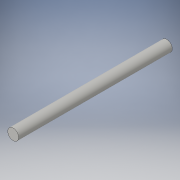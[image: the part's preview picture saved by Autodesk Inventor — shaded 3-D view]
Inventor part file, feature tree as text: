
AUTODESK INVENTOR PART (.ipt)
format: ipt  version: 2016 (Build 200138000, 138)  size: 86,528 bytes
history: native  units: in
note: dims shown in document units (in); Inventor stores cm internally (conversion verified against a paired STEP export)
features: extrude x1, sketch x1
ambient origin geometry x8: Origin, YZ Plane, XZ Plane, XY Plane, X Axis, Y Axis, Z Axis, Center Point
bodies: Solid1 (feature_tree)
feature tree (2):
  extrude  "Extrusion1"  Depth=1.5in TaperAngle=0.0deg
  sketch  "Sketch1"  dims[d0=0.107in d1=1.5in d2=0.0in]
